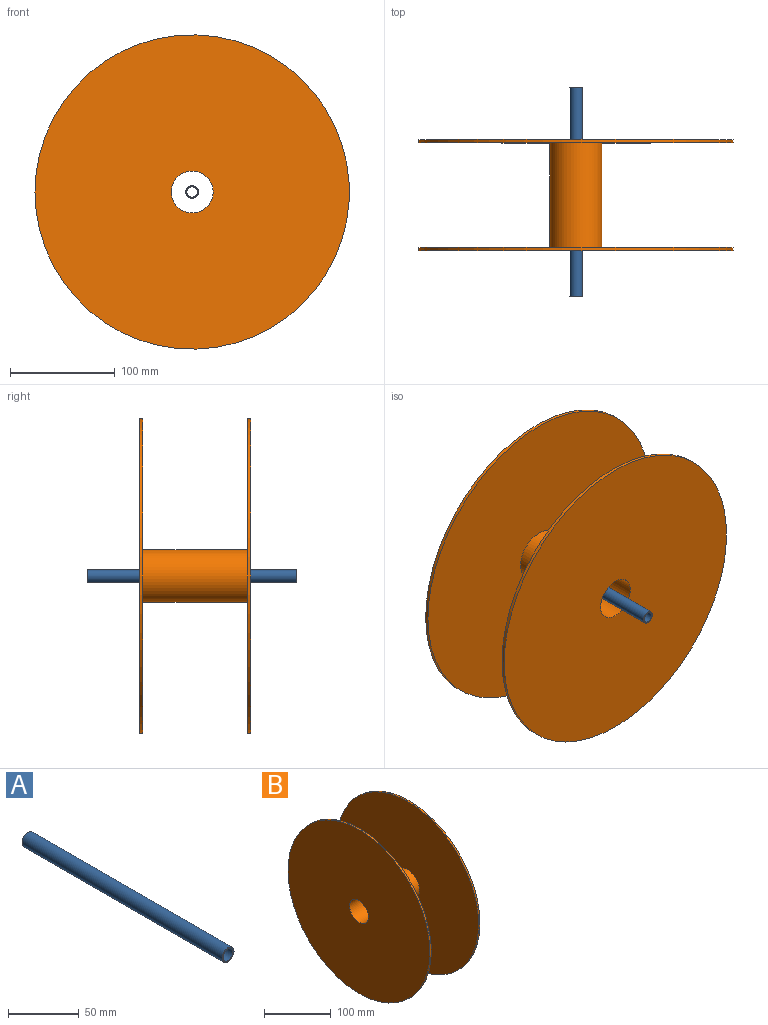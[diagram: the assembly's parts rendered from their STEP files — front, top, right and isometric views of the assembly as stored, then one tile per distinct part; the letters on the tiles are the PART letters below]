
ASSEMBLY  parts=2 mates=1
PART A: 4 faces, bbox 12x200x12 mm
  f0: cylinder r=5mm len=200mm, axis (0,1,0), area 6283.2mm2, adj f2,f3
  f1: cylinder r=6mm len=200mm, axis (0,1,0), area 7539.8mm2, adj f2,f3
  f2: plane 12x12mm, normal (0,-1,0), area 34.6mm2, adj f0,f1
  f3: plane 12x12mm, normal (0,1,0), area 34.6mm2, adj f0,f1
PART B: 8 faces, bbox 106x300x300 mm
  f0: cylinder r=25mm len=100mm, axis (-1,0,0), area 15708mm2, adj f1,f6
  f1: plane 300x300mm, normal (1,0,0), area 68722.3mm2, adj f0,f2
  f2: cylinder r=150mm len=300mm, axis (-1,0,0), area 2827.4mm2, adj f1,f3
  f3: plane 300x300mm, normal (-1,0,0), area 69429.2mm2, adj f2,f7
  f4: plane 300x300mm, normal (1,0,0), area 69429.2mm2, adj f5,f7
  f5: cylinder r=150mm len=300mm, axis (-1,0,0), area 2827.4mm2, adj f4,f6
  f6: plane 300x300mm, normal (-1,0,0), area 68722.3mm2, adj f0,f5
  f7: cylinder r=20mm len=106mm, axis (1,0,0), area 13320.4mm2, adj f3,f4
PLACE A t=(609.99,1253.25,828.34)mm
PLACE B rot(axis=(0.58,-0.58,-0.58),120deg) t=(609.99,1150.25,828.34)mm
MATE revolute B.f0 <-> A.f0  axis (0,1,0) through (609.99,1203.25,828.34)mm
